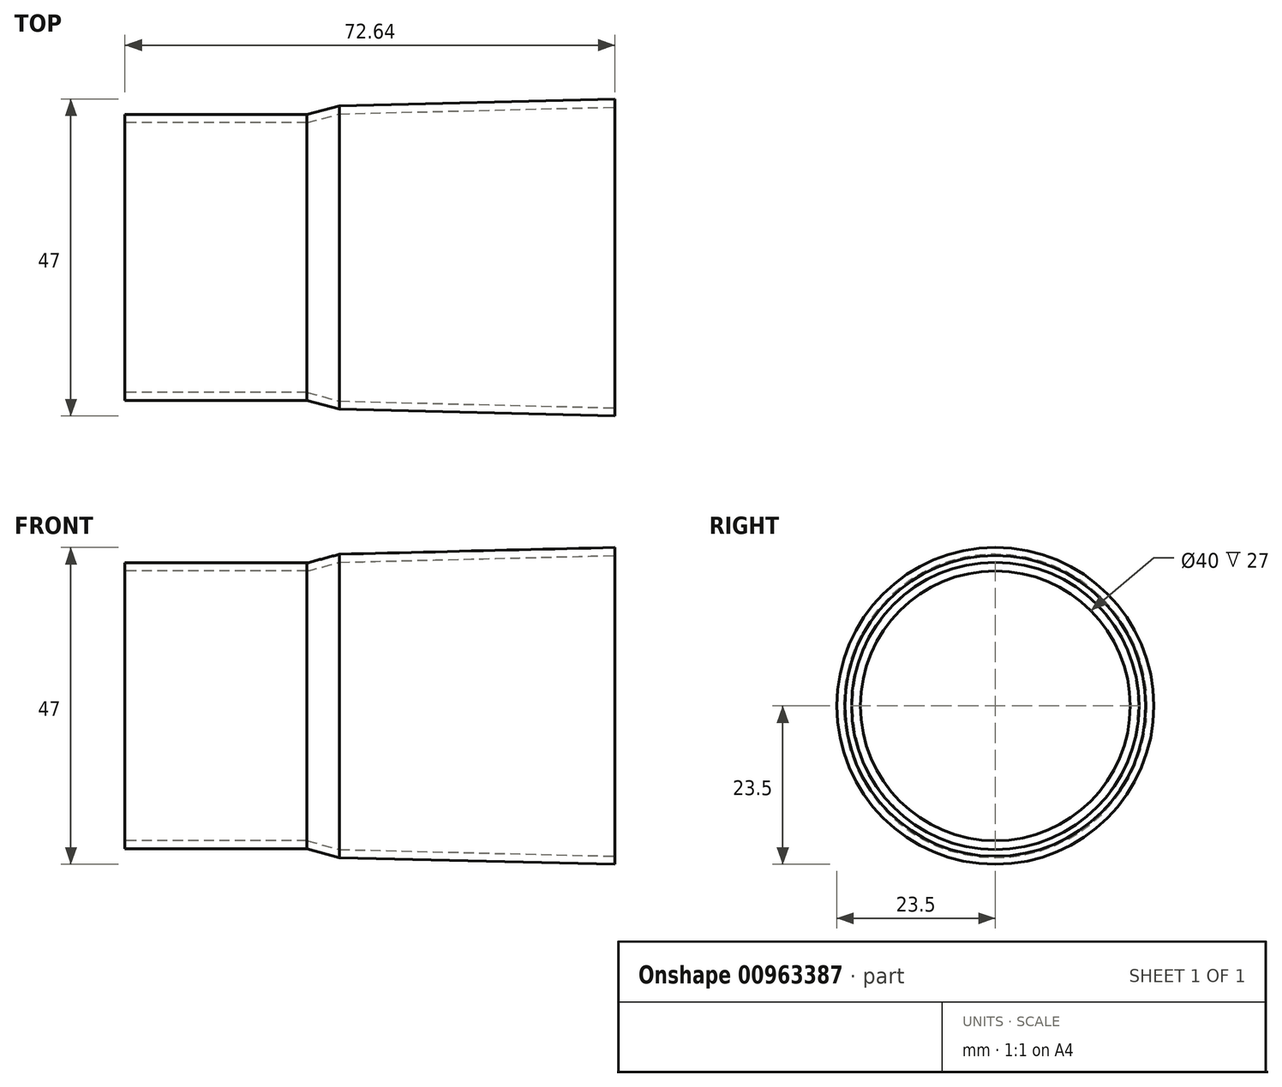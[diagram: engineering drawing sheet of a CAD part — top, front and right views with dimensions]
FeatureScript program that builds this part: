
annotation { "Feature Type Name" : "Feature", "Feature Type Description" : "" }
export const myFeature = defineFeature(function(context is Context, id is Id, definition is map)
    precondition{}
    {
        {
            var Q0;
            Q0=qCreatedBy(makeId("Top.planeOp"),FACE);
            var sketch = newSketch(context, id + "F0", { "sketchPlane" : qUnion([Q0])});
            skLineSegment(sketch, "E0", {"start": v(-2.47, 21.3) * mm, "end": v(-7.3, 20) * mm});
            skLineSegment(sketch, "E1", {"start": v(-34.3, 20) * mm, "end": v(-34.3, 21.2) * mm});
            skLineSegment(sketch, "E2", {"start": v(-7.3, 21.2) * mm, "end": v(-2.47, 22.5) * mm});
            skLineSegment(sketch, "E3", {"start": v(-43.34, 0) * mm, "end": v(39.1, 0) * mm, "construction": true});
            skLineSegment(sketch, "E4", {"start": v(-2.47, 22.5) * mm, "end": v(38.31, 23.5) * mm});
            skLineSegment(sketch, "E5", {"start": v(38.31, 23.5) * mm, "end": v(38.34, 22.3) * mm});
            skLineSegment(sketch, "E6", {"start": v(38.34, 22.3) * mm, "end": v(-2.47, 21.3) * mm});
            skPoint(sketch, "E7", {"position": v(38.34, 22.3) * mm});
            skPoint(sketch, "E8", {"position": v(17.94, 21.8) * mm});
            skPoint(sketch, "E9", {"position": v(-2.47, 21.3) * mm});
            skLineSegment(sketch, "E10", {"start": v(38.34, 22.3) * mm, "end": v(38.34, 0) * mm, "construction": true});
            skLineSegment(sketch, "E11", {"start": v(-2.47, 21.3) * mm, "end": v(-2.47, 0) * mm, "construction": true});
            skLineSegment(sketch, "E12", {"start": v(-34.3, 21.2) * mm, "end": v(-7.3, 21.2) * mm});
            skLineSegment(sketch, "E13", {"start": v(-34.3, 20) * mm, "end": v(-7.3, 20) * mm});
            skLineSegment(sketch, "E14", {"start": v(-2.47, 22.5) * mm, "end": v(-2.47, 21.3) * mm, "construction": true});
            skLineSegment(sketch, "E15", {"start": v(-7.3, 20) * mm, "end": v(-7.3, 0) * mm, "construction": true});
            skLineSegment(sketch, "E16", {"start": v(-7.3, 21.2) * mm, "end": v(-7.3, 20) * mm, "construction": true});
            skLineSegment(sketch, "E17", {"start": v(-34.3, 20) * mm, "end": v(-34.3, 0) * mm, "construction": true});
            skSolve(sketch);
        }
        {
            var Q0;
            Q0=makeQuery(id+"F0.imprint","IMPRINT",FACE,{"disambiguationData":[TD([[makeQuery(id+"F0.imprint","IMPRINT",EDGE,{"derivedFrom":sQuery(id+"F0.wireOp",EDGE,"E0")}),-1.0]])]});
            var Q1;
            Q1=sQuery(id+"F0.wireOp",EDGE,"E3");
            revolve(context, id + "F1", {"surfaceOperationType" : NewSurfaceOperationType.NEW, "entities" : qUnion([Q0]), "axis" : qUnion([Q1]), "revolveType" : RevolveType.FULL});
        }
    });
